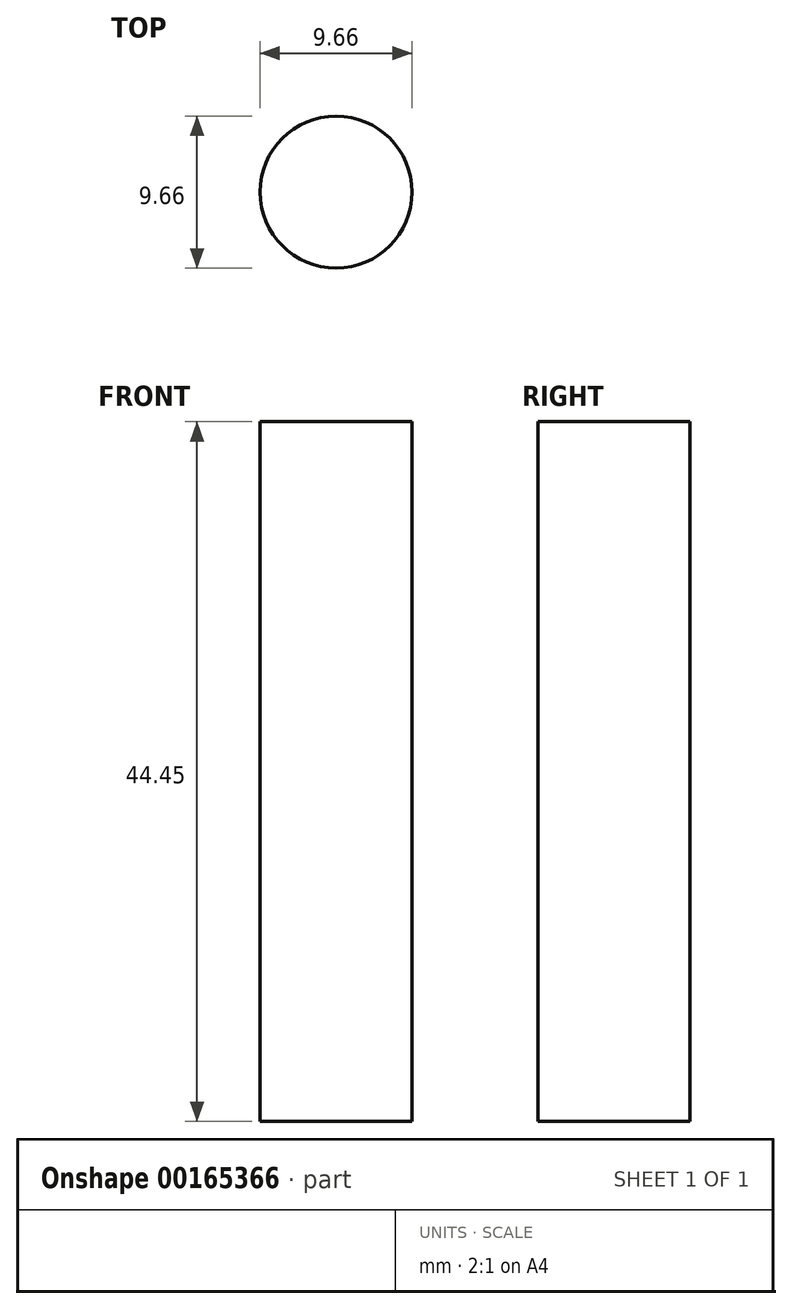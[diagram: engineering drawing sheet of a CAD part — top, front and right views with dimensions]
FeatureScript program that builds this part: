
annotation { "Feature Type Name" : "Feature", "Feature Type Description" : "" }
export const myFeature = defineFeature(function(context is Context, id is Id, definition is map)
    precondition{}
    {
        {
            var Q0;
            Q0=qCreatedBy(makeId("Top.planeOp"),FACE);
            var sketch = newSketch(context, id + "F0", { "sketchPlane" : qUnion([Q0])});
            skCircle(sketch, "E0", {"center": v(0, 0) * mm, "radius": 4.83 * mm});
            skSolve(sketch);
        }
        {
            var Q0;
            Q0=qSketchRegion(id+"F0",true);
            extrude(context, id + "F1", {"entities" : qUnion([Q0]), "depth" : 44.45 * mm});
        }
    });
